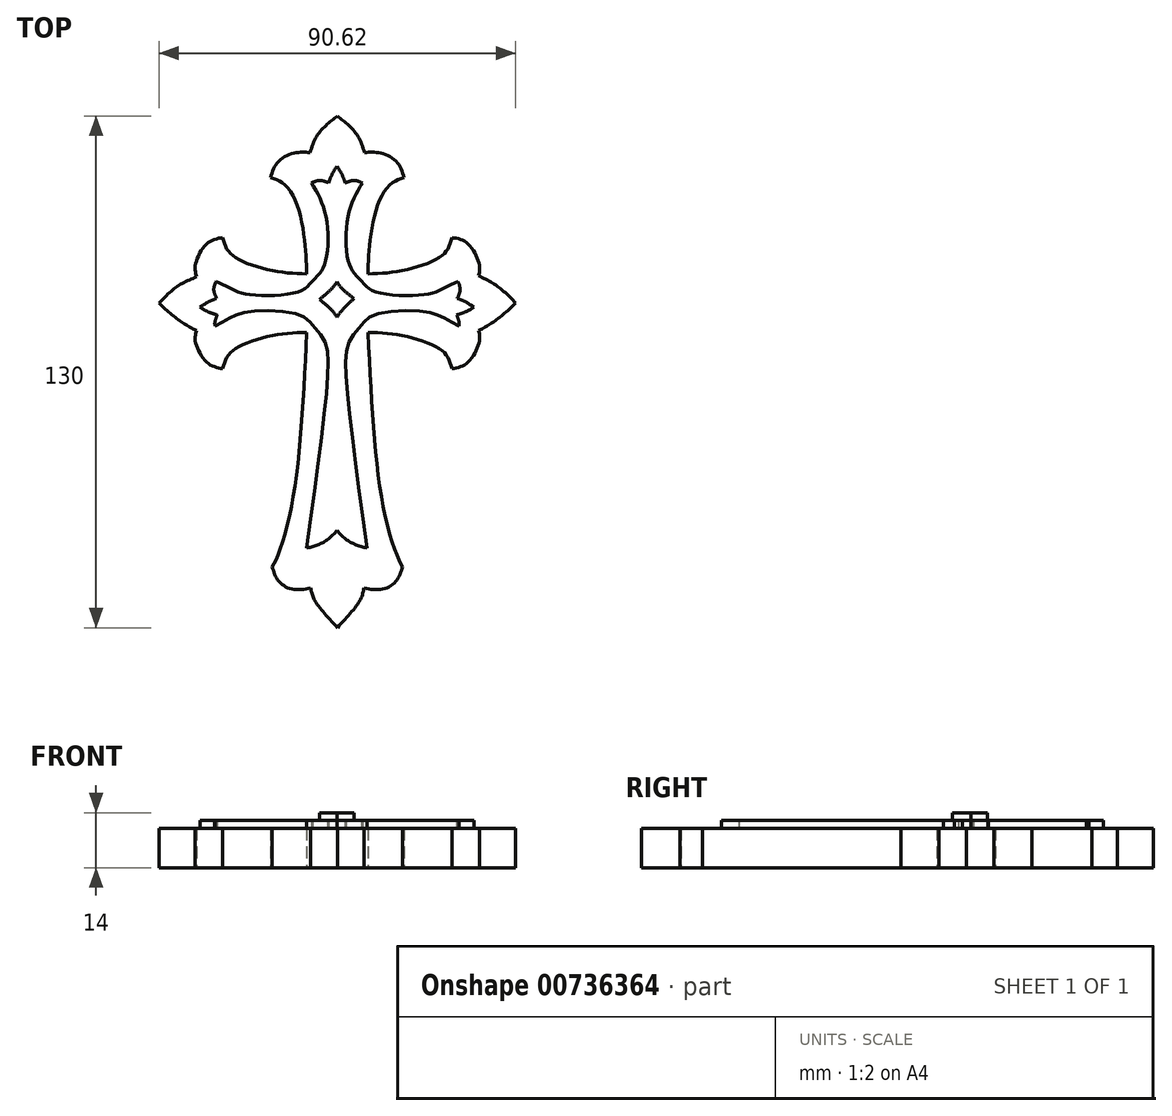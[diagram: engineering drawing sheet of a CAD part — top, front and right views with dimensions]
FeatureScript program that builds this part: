
annotation { "Feature Type Name" : "Feature", "Feature Type Description" : "" }
export const myFeature = defineFeature(function(context is Context, id is Id, definition is map)
    precondition{}
    {
        {
            var Q0;
            Q0=qCreatedBy(makeId("Top.planeOp"),FACE);
            var sketch = newSketch(context, id + "F0", { "sketchPlane" : qUnion([Q0])});
            skFitSpline(sketch, "E0", {"points": [v(0.1, 61.96) * mm, v(-2.47, 59.88) * mm, v(-5.1, 56.89) * mm, v(-6.83, 52.68) * mm], "startDerivative": vector(-8.37, -6.44) * mm, "endDerivative": vector(-4, -12.37) * mm});
            skFitSpline(sketch, "E1", {"points": [v(-6.83, 52.68) * mm, v(-10.25, 52.68) * mm, v(-14.8, 50.5) * mm, v(-16.87, 46.31) * mm], "startDerivative": vector(-10.9, 1.1) * mm, "endDerivative": vector(-4.19, -13.26) * mm});
            skFitSpline(sketch, "E2", {"points": [v(-16.87, 46.31) * mm, v(-13.87, 45) * mm, v(-10.3, 39.86) * mm, v(-8.1, 29.09) * mm, v(-7.67, 21.88) * mm], "startDerivative": vector(17.29, -5.19) * mm, "endDerivative": vector(0.9, -25.6) * mm});
            skFitSpline(sketch, "E3", {"points": [v(-7.67, 21.88) * mm, v(-16.36, 22.66) * mm, v(-24.94, 25.54) * mm, v(-27.88, 28.06) * mm, v(-29.02, 31.12) * mm], "startDerivative": vector(-27.95, 0.93) * mm, "endDerivative": vector(-4.72, 17.43) * mm, "construction": true});
            skFitSpline(sketch, "E4", {"points": [v(-29.02, 31.12) * mm, v(-32.98, 29.56) * mm, v(-35.98, 24.1) * mm, v(-35.7, 21.16) * mm], "startDerivative": vector(-12.4, -2.25) * mm, "endDerivative": vector(2.18, -8.92) * mm});
            skFitSpline(sketch, "E5", {"points": [v(-35.7, 21.16) * mm, v(-40.65, 18.64) * mm, v(-45.21, 14.44) * mm], "startDerivative": vector(-10.24, -5.05) * mm, "endDerivative": vector(-8.6, -8.83) * mm});
            skFitSpline(sketch, "E6", {"points": [v(-45.21, 14.44) * mm, v(-40.3, 10.19) * mm, v(-35.7, 7.49) * mm], "startDerivative": vector(9.2, -8.78) * mm, "endDerivative": vector(9.63, -4.57) * mm});
            skFitSpline(sketch, "E7.MirrorCS", {"points": [v(-29.02, -2.23) * mm, v(-32.98, -0.67) * mm, v(-35.98, 4.79) * mm, v(-35.7, 7.49) * mm], "startDerivative": vector(-12.4, 2.25) * mm, "endDerivative": vector(2.18, 8.92) * mm});
            skFitSpline(sketch, "E8.MirrorCS", {"points": [v(-7.67, 7) * mm, v(-16.36, 6.23) * mm, v(-24.94, 3.35) * mm, v(-27.88, 0.83) * mm, v(-29.02, -2.23) * mm], "startDerivative": vector(-27.95, -0.93) * mm, "endDerivative": vector(-4.72, -17.43) * mm, "construction": true});
            skFitSpline(sketch, "E9", {"points": [v(-7.67, 7) * mm, v(-9.47, -21.79) * mm, v(-12.27, -40.54) * mm, v(-15.2, -50.02) * mm, v(-16.45, -52.54) * mm], "startDerivative": vector(-4.02, -81.5) * mm, "endDerivative": vector(-10.3, -18.38) * mm});
            skFitSpline(sketch, "E10", {"points": [v(-16.45, -52.54) * mm, v(-15.01, -55.96) * mm, v(-11.6, -58.18) * mm, v(-6.67, -58) * mm], "startDerivative": vector(3.3, -11.57) * mm, "endDerivative": vector(14.15, 2.23) * mm});
            skFitSpline(sketch, "E11", {"points": [v(-6.67, -58) * mm, v(-5.62, -61.1) * mm, v(0.1, -68.04) * mm], "startDerivative": vector(1.59, -7.72) * mm, "endDerivative": vector(11.17, -12.02) * mm});
            skFitSpline(sketch, "E12.MirrorCS", {"points": [v(6.88, -58) * mm, v(5.83, -61.1) * mm, v(0.1, -68.04) * mm], "startDerivative": vector(-1.59, -7.72) * mm, "endDerivative": vector(-11.17, -12.02) * mm});
            skFitSpline(sketch, "E13.MirrorCS", {"points": [v(16.65, -52.54) * mm, v(15.21, -55.96) * mm, v(11.8, -58.18) * mm, v(6.88, -58) * mm], "startDerivative": vector(-3.3, -11.57) * mm, "endDerivative": vector(-14.15, 2.23) * mm});
            skFitSpline(sketch, "E14.MirrorCS", {"points": [v(7.87, 7) * mm, v(9.67, -21.79) * mm, v(12.47, -40.54) * mm, v(15.4, -50.02) * mm, v(16.65, -52.54) * mm], "startDerivative": vector(4.02, -81.5) * mm, "endDerivative": vector(10.3, -18.38) * mm});
            skFitSpline(sketch, "E15.MirrorCS", {"points": [v(17.07, 46.31) * mm, v(14.07, 45) * mm, v(10.5, 39.86) * mm, v(8.3, 29.09) * mm, v(7.87, 21.88) * mm], "startDerivative": vector(-17.29, -5.19) * mm, "endDerivative": vector(-0.9, -25.6) * mm});
            skFitSpline(sketch, "E16.MirrorCS", {"points": [v(7.87, 21.88) * mm, v(16.57, 22.66) * mm, v(25.14, 25.54) * mm, v(28.08, 28.06) * mm, v(29.22, 31.12) * mm], "startDerivative": vector(27.95, 0.93) * mm, "endDerivative": vector(4.72, 17.43) * mm, "construction": true});
            skFitSpline(sketch, "E17.MirrorCS", {"points": [v(7.87, 7) * mm, v(16.57, 6.23) * mm, v(25.14, 3.35) * mm, v(28.08, 0.83) * mm, v(29.22, -2.23) * mm], "startDerivative": vector(27.95, -0.93) * mm, "endDerivative": vector(4.72, -17.43) * mm, "construction": true});
            skFitSpline(sketch, "E18.MirrorCS", {"points": [v(29.22, -2.23) * mm, v(33.18, -0.67) * mm, v(36.18, 4.79) * mm, v(36, 7.49) * mm], "startDerivative": vector(12.4, 2.25) * mm, "endDerivative": vector(-2.18, 8.92) * mm});
            skFitSpline(sketch, "E19.MirrorCS", {"points": [v(45.41, 14.44) * mm, v(40.5, 10.19) * mm, v(36, 7.49) * mm], "startDerivative": vector(-9.2, -8.78) * mm, "endDerivative": vector(-9.63, -4.57) * mm});
            skFitSpline(sketch, "E20.MirrorCS", {"points": [v(36, 21.4) * mm, v(40.86, 18.64) * mm, v(45.41, 14.44) * mm], "startDerivative": vector(10.24, -5.05) * mm, "endDerivative": vector(8.6, -8.83) * mm});
            skFitSpline(sketch, "E21.MirrorCS", {"points": [v(29.22, 31.12) * mm, v(33.18, 29.56) * mm, v(36.18, 24.1) * mm, v(36, 21.4) * mm], "startDerivative": vector(12.4, -2.25) * mm, "endDerivative": vector(-2.18, -8.92) * mm});
            skFitSpline(sketch, "E22.MirrorCS", {"points": [v(0.1, 61.96) * mm, v(2.67, 59.88) * mm, v(5.31, 56.89) * mm, v(7.03, 52.68) * mm], "startDerivative": vector(8.37, -6.44) * mm, "endDerivative": vector(4, -12.37) * mm});
            skFitSpline(sketch, "E23.MirrorCS", {"points": [v(7.03, 52.68) * mm, v(10.46, 52.68) * mm, v(15, 50.5) * mm, v(17.07, 46.31) * mm], "startDerivative": vector(10.9, 1.1) * mm, "endDerivative": vector(4.19, -13.26) * mm});
            skFitSpline(sketch, "E24", {"points": [v(-7.67, 7) * mm, v(-16.36, 6.23) * mm, v(-24.94, 3.35) * mm, v(-27.88, 0.83) * mm, v(-29.02, -2.23) * mm], "startDerivative": vector(-27.95, -0.93) * mm, "endDerivative": vector(-4.72, -17.43) * mm});
            skFitSpline(sketch, "E25", {"points": [v(-7.67, 21.88) * mm, v(-16.36, 22.66) * mm, v(-24.94, 25.54) * mm, v(-27.88, 28.06) * mm, v(-29.02, 31.12) * mm], "startDerivative": vector(-27.95, 0.93) * mm, "endDerivative": vector(-4.72, 17.43) * mm});
            skFitSpline(sketch, "E26", {"points": [v(7.87, 21.88) * mm, v(16.57, 22.66) * mm, v(25.14, 25.54) * mm, v(28.08, 28.06) * mm, v(29.22, 31.12) * mm], "startDerivative": vector(27.95, 0.93) * mm, "endDerivative": vector(4.72, 17.43) * mm});
            skFitSpline(sketch, "E27", {"points": [v(7.87, 7) * mm, v(16.57, 6.23) * mm, v(25.14, 3.35) * mm, v(28.08, 0.83) * mm, v(29.22, -2.23) * mm], "startDerivative": vector(27.95, -0.93) * mm, "endDerivative": vector(4.72, -17.43) * mm});
            skPoint(sketch, "E28", {"position": v(0, 15.4) * mm});
            skFitSpline(sketch, "E29", {"points": [v(0, 19.87) * mm, v(-1.75, 17.7) * mm, v(-4.37, 15.36) * mm], "startDerivative": vector(-3.24, -5.58) * mm, "endDerivative": vector(-4.78, -4.38) * mm});
            skFitSpline(sketch, "E30.MirrorCS", {"points": [v(0, 19.87) * mm, v(1.75, 17.7) * mm, v(4.3, 15.6) * mm], "startDerivative": vector(3.24, -5.58) * mm, "endDerivative": vector(4.78, -4.38) * mm});
            skFitSpline(sketch, "E31.MirrorCS", {"points": [v(0, 10.85) * mm, v(-1.75, 13.1) * mm, v(-4.37, 15.36) * mm], "startDerivative": vector(-3.24, 5.58) * mm, "endDerivative": vector(-4.78, 4.38) * mm});
            skFitSpline(sketch, "E32.MirrorCS", {"points": [v(0, 10.85) * mm, v(1.75, 13.1) * mm, v(4.3, 15.6) * mm], "startDerivative": vector(3.24, 5.58) * mm, "endDerivative": vector(4.78, 4.38) * mm});
            skFitSpline(sketch, "E33", {"points": [v(-6.25, 20) * mm, v(-3.18, 24.12) * mm, v(-2.82, 36.54) * mm, v(-6.45, 44.96) * mm], "startDerivative": vector(15.23, 18.12) * mm, "endDerivative": vector(-12.48, 21.63) * mm});
            skFitSpline(sketch, "E34", {"points": [v(-6.45, 44.96) * mm, v(-4.41, 45.63) * mm, v(-2.08, 44.96) * mm], "startDerivative": vector(4.12, 2.04) * mm, "endDerivative": vector(4.6, -2) * mm});
            skFitSpline(sketch, "E35", {"points": [v(-2.08, 44.96) * mm, v(-1.28, 47.14) * mm, v(0, 49.24) * mm], "startDerivative": vector(1.42, 4.5) * mm, "endDerivative": vector(2.74, 4.07) * mm});
            skFitSpline(sketch, "E36.MirrorCS", {"points": [v(2.08, 44.96) * mm, v(1.28, 47.14) * mm, v(0, 49.24) * mm], "startDerivative": vector(-1.42, 4.5) * mm, "endDerivative": vector(-2.74, 4.07) * mm});
            skFitSpline(sketch, "E37.MirrorCS", {"points": [v(6.45, 44.96) * mm, v(4.41, 45.63) * mm, v(2.08, 44.96) * mm], "startDerivative": vector(-4.12, 2.04) * mm, "endDerivative": vector(-4.6, -2) * mm});
            skFitSpline(sketch, "E38.MirrorCS", {"points": [v(6.25, 20) * mm, v(3.18, 24.12) * mm, v(2.82, 36.54) * mm, v(6.45, 44.96) * mm], "startDerivative": vector(-15.23, 18.12) * mm, "endDerivative": vector(12.48, 21.63) * mm});
            skFitSpline(sketch, "E39.MirrorCS", {"points": [v(-30.7, 19.97) * mm, v(-31.3, 17.91) * mm, v(-30.56, 15.6) * mm], "startDerivative": vector(-1.91, -4.18) * mm, "endDerivative": vector(2.13, -4.54) * mm});
            skFitSpline(sketch, "E40.MirrorCS", {"points": [v(-30.56, 15.6) * mm, v(-32.72, 14.73) * mm, v(-34.78, 13.4) * mm], "startDerivative": vector(-4.45, -1.55) * mm, "endDerivative": vector(-3.98, -2.87) * mm});
            skFitSpline(sketch, "E41.MirrorCS", {"points": [v(-30.44, 11.44) * mm, v(-32.64, 12.18) * mm, v(-34.78, 13.4) * mm], "startDerivative": vector(-4.54, 1.28) * mm, "endDerivative": vector(-4.15, 2.62) * mm});
            skFitSpline(sketch, "E42.MirrorCS", {"points": [v(-30.3, 7.08) * mm, v(-31.04, 9.1) * mm, v(-30.44, 11.44) * mm], "startDerivative": vector(-2.16, 4.06) * mm, "endDerivative": vector(1.86, 4.66) * mm});
            skFitSpline(sketch, "E43", {"points": [v(-6.25, 20) * mm, v(-9.77, 17.33) * mm, v(-22.17, 16.6) * mm, v(-26.78, 18.02) * mm, v(-30.7, 19.97) * mm], "startDerivative": vector(-16.49, -16.49) * mm, "endDerivative": vector(-19.08, 9.64) * mm});
            skFitSpline(sketch, "E44.MirrorCS", {"points": [v(-6.25, 8.9) * mm, v(-9.77, 11.56) * mm, v(-22.17, 12.3) * mm, v(-26.78, 10.87) * mm, v(-30.7, 8.92) * mm], "startDerivative": vector(-16.49, 16.49) * mm, "endDerivative": vector(-19.08, -9.64) * mm, "construction": true});
            skFitSpline(sketch, "E45.MirrorCS", {"points": [v(6.25, 20) * mm, v(9.77, 17.33) * mm, v(22.17, 16.6) * mm, v(26.78, 18.02) * mm, v(30.7, 19.97) * mm], "startDerivative": vector(16.49, -16.49) * mm, "endDerivative": vector(19.08, 9.64) * mm});
            skFitSpline(sketch, "E46.MirrorCS", {"points": [v(30.7, 19.97) * mm, v(31.3, 17.91) * mm, v(30.56, 15.6) * mm], "startDerivative": vector(1.91, -4.18) * mm, "endDerivative": vector(-2.13, -4.54) * mm});
            skFitSpline(sketch, "E47.MirrorCS", {"points": [v(30.56, 15.6) * mm, v(32.72, 14.73) * mm, v(34.78, 13.4) * mm], "startDerivative": vector(4.45, -1.55) * mm, "endDerivative": vector(3.98, -2.87) * mm});
            skFitSpline(sketch, "E48.MirrorCS", {"points": [v(30.44, 11.44) * mm, v(32.64, 12.18) * mm, v(34.78, 13.4) * mm], "startDerivative": vector(4.54, 1.28) * mm, "endDerivative": vector(4.15, 2.62) * mm});
            skFitSpline(sketch, "E49", {"points": [v(-30.97, 8.63) * mm, v(-26.78, 10.87) * mm, v(-22.17, 12.3) * mm, v(-9.77, 11.56) * mm, v(-6.25, 8.9) * mm, v(-3.18, 4.77) * mm, v(-2.35, -4.24) * mm, v(-7.67, -47.82) * mm], "startDerivative": vector(43.58, 24.04) * mm, "endDerivative": vector(-23.32, -169.8) * mm});
            skFitSpline(sketch, "E50", {"points": [v(-7.67, -47.82) * mm, v(-3.18, -46.16) * mm, v(0, -43.37) * mm], "startDerivative": vector(9.26, 2.55) * mm, "endDerivative": vector(6.03, 6.39) * mm});
            skFitSpline(sketch, "E51.MirrorCS", {"points": [v(7.67, -47.82) * mm, v(3.18, -46.16) * mm, v(0, -43.37) * mm], "startDerivative": vector(-9.26, 2.55) * mm, "endDerivative": vector(-6.03, 6.39) * mm});
            skFitSpline(sketch, "E52.MirrorCS", {"points": [v(30.97, 8.63) * mm, v(26.78, 10.87) * mm, v(22.17, 12.3) * mm, v(9.77, 11.56) * mm, v(6.25, 8.9) * mm, v(3.18, 4.77) * mm, v(2.35, -4.24) * mm, v(7.67, -47.82) * mm], "startDerivative": vector(-43.58, 24.04) * mm, "endDerivative": vector(23.32, -169.8) * mm});
            skFitSpline(sketch, "E53.MirrorCS", {"points": [v(30.3, 7.08) * mm, v(31.04, 9.1) * mm, v(30.44, 11.44) * mm], "startDerivative": vector(2.16, 4.06) * mm, "endDerivative": vector(-1.86, 4.66) * mm});
            skSolve(sketch);
        }
        {
            var Q0;
            Q0=makeQuery(id+"F0.imprint","IMPRINT",FACE,{"disambiguationData":[TD([[makeQuery(id+"F0.imprint","IMPRINT",EDGE,{"derivedFrom":sQuery(id+"F0.wireOp",EDGE,"E0")}),1.0]])]});
            var Q1;
            Q1=makeQuery(id+"F0.imprint","IMPRINT",FACE,{"disambiguationData":[TD([[makeQuery(id+"F0.imprint","IMPRINT",EDGE,{"derivedFrom":sQuery(id+"F0.wireOp",EDGE,"E29")}),1.0]])]});
            var Q2;
            Q2=makeQuery(id+"F0.imprint","IMPRINT",FACE,{"disambiguationData":[TD([[makeQuery(id+"F0.imprint","IMPRINT",EDGE,{"derivedFrom":sQuery(id+"F0.wireOp",EDGE,"E29")}),-1.0]])]});
            extrude(context, id + "F1", {"entities" : qUnion([Q0, Q1, Q2]), "depth" : 10 * mm, "offsetDistance" : 25 * mm});
        }
        {
            var Q0;
            Q0=makeQuery(id+"F0.imprint","IMPRINT",FACE,{"disambiguationData":[TD([[makeQuery(id+"F0.imprint","IMPRINT",EDGE,{"derivedFrom":sQuery(id+"F0.wireOp",EDGE,"E29")}),-1.0]])]});
            extrude(context, id + "F2", {"entities" : qUnion([Q0]), "operationType" : NewBodyOperationType.ADD, "depth" : 12 * mm, "offsetDistance" : 25 * mm});
        }
        {
            var Q0;
            Q0=makeQuery(id+"F0.imprint","IMPRINT",FACE,{"disambiguationData":[TD([[makeQuery(id+"F0.imprint","IMPRINT",EDGE,{"derivedFrom":sQuery(id+"F0.wireOp",EDGE,"E29")}),1.0]])]});
            extrude(context, id + "F3", {"entities" : qUnion([Q0]), "operationType" : NewBodyOperationType.ADD, "depth" : 14 * mm, "offsetDistance" : 25 * mm});
        }
    });
